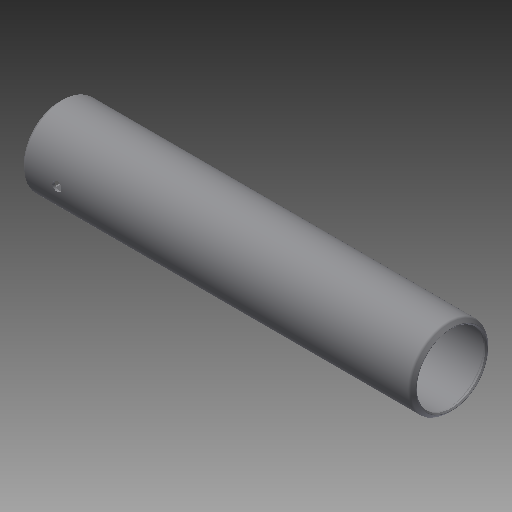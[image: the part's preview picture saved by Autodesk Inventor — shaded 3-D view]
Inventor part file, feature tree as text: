
AUTODESK INVENTOR PART (.ipt)
format: ipt  version: 2018.3 (Build 223284000, 284)  size: 164,352 bytes
history: native  units: in
note: dims shown in document units (in); Inventor stores cm internally (conversion verified against a paired STEP export)
features: other x42, sketch x2, revolve x1, extrude x1
ambient origin geometry x8: Origin, YZ Plane, XZ Plane, XY Plane, X Axis, Y Axis, Z Axis, Center Point
bodies: Solid1 (feature_tree)
feature tree (46):
  revolve  "Revolution1"  [1 undecoded]
  extrude  "Extrusion1"  [1 undecoded]
  other  "cp1_XY"
  other  "cp1_YZ"
  other  "cp1_ZX"
  other  "cp1_X"
  other  "cp1_Y"
  other  "cp1_Z"
  other  "cp1_Center"
  other  "cp2_XY"
  other  "cp2_YZ"
  other  "cp2_ZX"
  other  "cp2_X"
  other  "cp2_Y"
  other  "cp2_Z"
  other  "cp2_Center"
  other  "cp3_XY"
  other  "cp3_YZ"
  other  "cp3_ZX"
  other  "cp3_X"
  other  "cp3_Y"
  other  "cp3_Z"
  other  "cp3_Center"
  other  "cp4_XY"
  other  "cp4_YZ"
  other  "cp4_ZX"
  other  "cp4_X"
  other  "cp4_Y"
  other  "cp4_Z"
  other  "cp4_Center"
  other  "tube_front_XY"
  other  "tube_front_YZ"
  other  "tube_front_ZX"
  other  "tube_front_X"
  other  "tube_front_Y"
  other  "tube_front_Z"
  other  "tube_front_Center"
  other  "tube_rear_XY"
  other  "tube_rear_YZ"
  other  "tube_rear_ZX"
  other  "tube_rear_X"
  other  "tube_rear_Y"
  other  "tube_rear_Z"
  other  "tube_rear_Center"
  sketch  "Sketch_1"  dims[d0=360.0deg d1=0.4025in d2=0.0in]
  sketch  "Sketch_4"
note: 2 required parameter values undecoded (feature->parameter linkage not recoverable at this tier; creation-order binding heuristic only, values carry confidence <= 0.55)